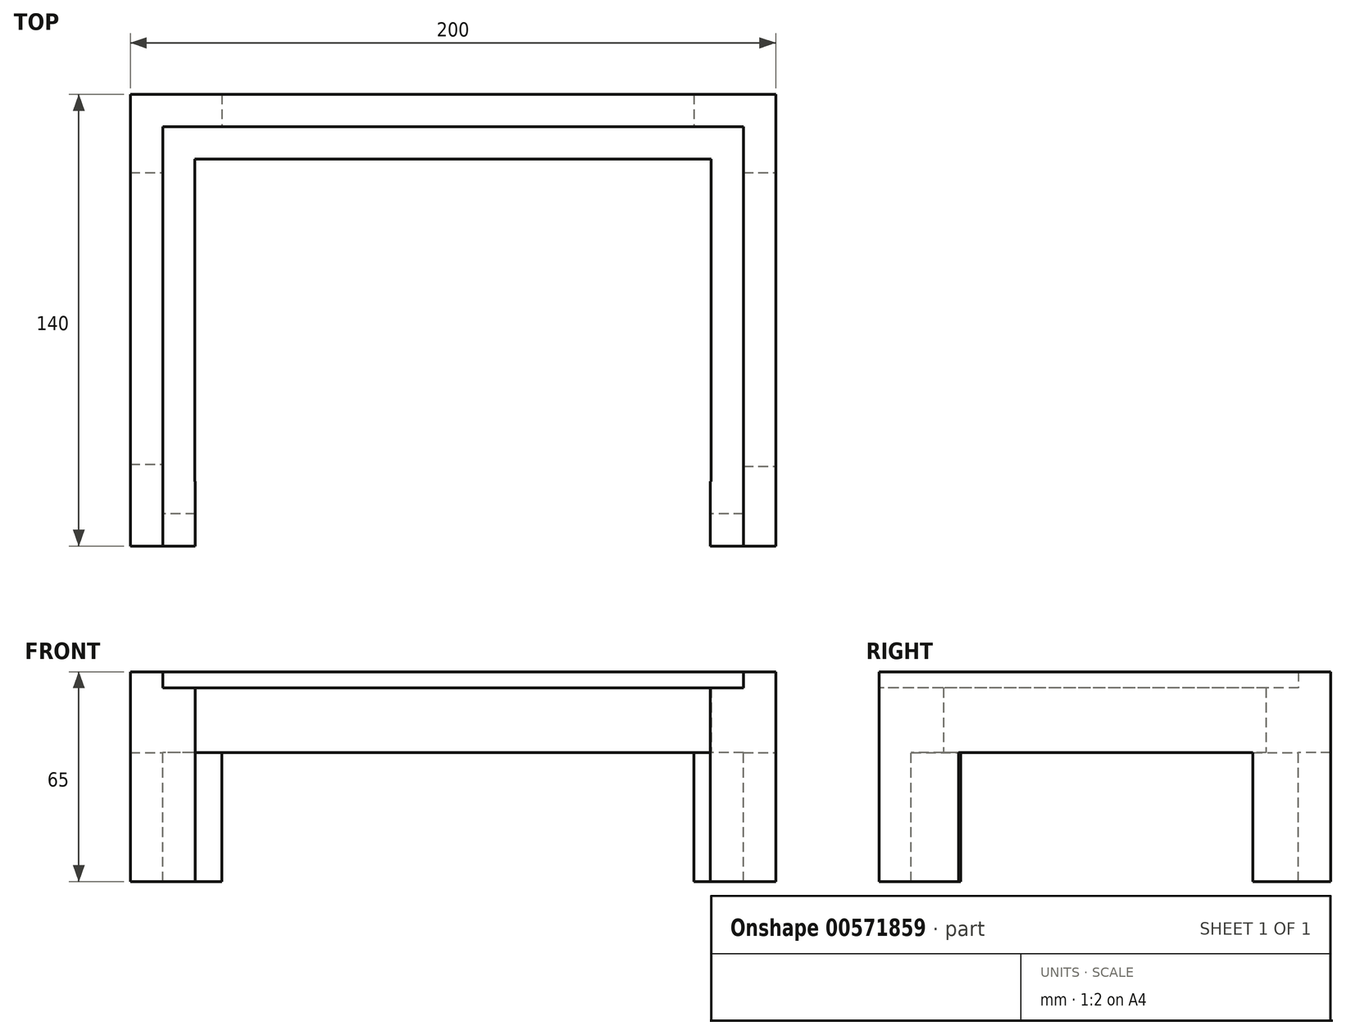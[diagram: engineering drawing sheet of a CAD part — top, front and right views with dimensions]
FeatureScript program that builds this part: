
annotation { "Feature Type Name" : "Feature", "Feature Type Description" : "" }
export const myFeature = defineFeature(function(context is Context, id is Id, definition is map)
    precondition{}
    {
        {
            var Q0;
            Q0=qCreatedBy(makeId("Top.planeOp"),FACE);
            var sketch = newSketch(context, id + "F0", { "sketchPlane" : qUnion([Q0])});
            skLineSegment(sketch, "E0.left", {"start": v(90, 0) * mm, "end": v(90, 0) * mm});
            skLineSegment(sketch, "E0.right", {"start": v(-90, 0) * mm, "end": v(-90, 0) * mm});
            skPoint(sketch, "E0.middle", {"position": v(0, 0) * mm});
            skLineSegment(sketch, "E1.bottom", {"start": v(100, -70) * mm, "end": v(-100, -70) * mm});
            skLineSegment(sketch, "E1.top", {"start": v(100, 70) * mm, "end": v(-100, 70) * mm});
            skLineSegment(sketch, "E1.left", {"start": v(100, -70) * mm, "end": v(100, 70) * mm});
            skLineSegment(sketch, "E1.right", {"start": v(-100, -70) * mm, "end": v(-100, 70) * mm});
            skLineSegment(sketch, "E2.bottom", {"start": v(90, -60) * mm, "end": v(-90, -60) * mm});
            skLineSegment(sketch, "E2.top", {"start": v(90, 60) * mm, "end": v(-90, 60) * mm});
            skLineSegment(sketch, "E2.left", {"start": v(90, -60) * mm, "end": v(90, 60) * mm});
            skLineSegment(sketch, "E2.right", {"start": v(-90, -60) * mm, "end": v(-90, 60) * mm});
            skLineSegment(sketch, "E3", {"start": v(-100, 45.82) * mm, "end": v(-90, 45.82) * mm});
            skLineSegment(sketch, "E4", {"start": v(-71.68, 70) * mm, "end": v(-71.68, 60) * mm});
            skLineSegment(sketch, "E5", {"start": v(-100, -44.62) * mm, "end": v(-90, -44.62) * mm});
            skLineSegment(sketch, "E6", {"start": v(90, -45.29) * mm, "end": v(100, -45.29) * mm});
            skLineSegment(sketch, "E7", {"start": v(74.62, 70) * mm, "end": v(74.62, 60) * mm});
            skLineSegment(sketch, "E8", {"start": v(90, 45.82) * mm, "end": v(100, 45.82) * mm});
            skLineSegment(sketch, "E9.bottom", {"start": v(80, 50) * mm, "end": v(-80, 50) * mm});
            skLineSegment(sketch, "E9.top", {"start": v(80, -50) * mm, "end": v(-80, -50) * mm});
            skLineSegment(sketch, "E9.left", {"start": v(80, 50) * mm, "end": v(80, -50) * mm});
            skLineSegment(sketch, "E9.right", {"start": v(-80, 50) * mm, "end": v(-80, -50) * mm});
            skLineSegment(sketch, "E10.bottom", {"start": v(79.75, -50) * mm, "end": v(-79.88, -50) * mm});
            skLineSegment(sketch, "E10.top", {"start": v(79.75, -70) * mm, "end": v(-79.88, -70) * mm});
            skLineSegment(sketch, "E10.left", {"start": v(79.75, -50) * mm, "end": v(79.75, -70) * mm});
            skLineSegment(sketch, "E10.right", {"start": v(-79.88, -50) * mm, "end": v(-79.88, -70) * mm});
            skLineSegment(sketch, "E11", {"start": v(-90, -60) * mm, "end": v(-90, -70) * mm});
            skLineSegment(sketch, "E12", {"start": v(90, -60) * mm, "end": v(90, -70) * mm});
            skSolve(sketch);
        }
        {
            var Q0;
            {var subQ4=sQuery(id+"F0.wireOp",EDGE,"E7");Q0=makeQuery(id+"F0.imprint","IMPRINT",FACE,{"disambiguationData":[TD([[makeQuery(id+"F0.imprint","IMPRINT",EDGE,{"derivedFrom":subQ4}),1.0]])]});}
            var Q1;
            {var subQ0=sQuery(id+"F0.wireOp",EDGE,"E6");Q1=makeQuery(id+"F0.imprint","IMPRINT",FACE,{"disambiguationData":[TD([[makeQuery(id+"F0.imprint","IMPRINT",EDGE,{"derivedFrom":subQ0}),1.0]])]});}
            var Q2;
            Q2=makeQuery(id+"F0.imprint","IMPRINT",FACE,{"disambiguationData":[TD([[makeQuery(id+"F0.imprint","IMPRINT",EDGE,{"derivedFrom":sQuery(id+"F0.wireOp",EDGE,"E9.bottom")}),-1.0]])]});
            var Q3;
            {var subQ0=sQuery(id+"F0.wireOp",EDGE,"E6");Q3=makeQuery(id+"F0.imprint","IMPRINT",FACE,{"disambiguationData":[TD([[makeQuery(id+"F0.imprint","IMPRINT",EDGE,{"derivedFrom":subQ0}),-1.0]])]});}
            var Q4;
            {var subQ3=sQuery(id+"F0.wireOp",EDGE,"E12");Q4=makeQuery(id+"F0.imprint","IMPRINT",FACE,{"disambiguationData":[TD([[makeQuery(id+"F0.imprint","IMPRINT",EDGE,{"derivedFrom":subQ3}),-1.0]])]});}
            var Q5;
            {var subQ0=sQuery(id+"F0.wireOp",EDGE,"E5");Q5=makeQuery(id+"F0.imprint","IMPRINT",FACE,{"disambiguationData":[TD([[makeQuery(id+"F0.imprint","IMPRINT",EDGE,{"derivedFrom":subQ0}),-1.0]])]});}
            var Q6;
            {var subQ3=sQuery(id+"F0.wireOp",EDGE,"E11");Q6=makeQuery(id+"F0.imprint","IMPRINT",FACE,{"disambiguationData":[TD([[makeQuery(id+"F0.imprint","IMPRINT",EDGE,{"derivedFrom":subQ3}),1.0]])]});}
            var Q7;
            {var subQ0=sQuery(id+"F0.wireOp",EDGE,"E3");Q7=makeQuery(id+"F0.imprint","IMPRINT",FACE,{"disambiguationData":[TD([[makeQuery(id+"F0.imprint","IMPRINT",EDGE,{"derivedFrom":subQ0}),-1.0]])]});}
            var Q8;
            {var subQ3=sQuery(id+"F0.wireOp",EDGE,"E3");Q8=makeQuery(id+"F0.imprint","IMPRINT",FACE,{"disambiguationData":[TD([[makeQuery(id+"F0.imprint","IMPRINT",EDGE,{"derivedFrom":subQ3}),1.0]])]});}
            var Q9;
            {var subQ0=sQuery(id+"F0.wireOp",EDGE,"E4");Q9=makeQuery(id+"F0.imprint","IMPRINT",FACE,{"disambiguationData":[TD([[makeQuery(id+"F0.imprint","IMPRINT",EDGE,{"derivedFrom":subQ0}),1.0]])]});}
            extrude(context, id + "F1", {"entities" : qUnion([Q0, Q1, Q2, Q3, Q4, Q5, Q6, Q7, Q8, Q9]), "depth" : 20 * mm, "offsetDistance" : 25 * mm});
        }
        {
            var Q0;
            {var subQ3=sQuery(id+"F0.wireOp",EDGE,"E3");Q0=makeQuery(id+"F0.imprint","IMPRINT",FACE,{"disambiguationData":[TD([[makeQuery(id+"F0.imprint","IMPRINT",EDGE,{"derivedFrom":subQ3}),1.0]])]});}
            var Q1;
            {var subQ0=sQuery(id+"F0.wireOp",EDGE,"E3");Q1=makeQuery(id+"F0.imprint","IMPRINT",FACE,{"disambiguationData":[TD([[makeQuery(id+"F0.imprint","IMPRINT",EDGE,{"derivedFrom":subQ0}),-1.0]])]});}
            var Q2;
            {var subQ0=sQuery(id+"F0.wireOp",EDGE,"E5");Q2=makeQuery(id+"F0.imprint","IMPRINT",FACE,{"disambiguationData":[TD([[makeQuery(id+"F0.imprint","IMPRINT",EDGE,{"derivedFrom":subQ0}),-1.0]])]});}
            var Q3;
            {var subQ0=sQuery(id+"F0.wireOp",EDGE,"E4");Q3=makeQuery(id+"F0.imprint","IMPRINT",FACE,{"disambiguationData":[TD([[makeQuery(id+"F0.imprint","IMPRINT",EDGE,{"derivedFrom":subQ0}),1.0]])]});}
            var Q4;
            {var subQ4=sQuery(id+"F0.wireOp",EDGE,"E7");Q4=makeQuery(id+"F0.imprint","IMPRINT",FACE,{"disambiguationData":[TD([[makeQuery(id+"F0.imprint","IMPRINT",EDGE,{"derivedFrom":subQ4}),1.0]])]});}
            var Q5;
            {var subQ0=sQuery(id+"F0.wireOp",EDGE,"E6");Q5=makeQuery(id+"F0.imprint","IMPRINT",FACE,{"disambiguationData":[TD([[makeQuery(id+"F0.imprint","IMPRINT",EDGE,{"derivedFrom":subQ0}),1.0]])]});}
            var Q6;
            {var subQ0=sQuery(id+"F0.wireOp",EDGE,"E6");Q6=makeQuery(id+"F0.imprint","IMPRINT",FACE,{"disambiguationData":[TD([[makeQuery(id+"F0.imprint","IMPRINT",EDGE,{"derivedFrom":subQ0}),-1.0]])]});}
            extrude(context, id + "F2", {"entities" : qUnion([Q0, Q1, Q2, Q3, Q4, Q5, Q6]), "operationType" : NewBodyOperationType.ADD, "depth" : 25 * mm, "offsetDistance" : 25 * mm});
        }
        {
            var Q0;
            {var subQ3=sQuery(id+"F0.wireOp",EDGE,"E3");Q0=makeQuery(id+"F0.imprint","IMPRINT",FACE,{"disambiguationData":[TD([[makeQuery(id+"F0.imprint","IMPRINT",EDGE,{"derivedFrom":subQ3}),1.0]])]});}
            var Q1;
            {var subQ0=sQuery(id+"F0.wireOp",EDGE,"E5");Q1=makeQuery(id+"F0.imprint","IMPRINT",FACE,{"disambiguationData":[TD([[makeQuery(id+"F0.imprint","IMPRINT",EDGE,{"derivedFrom":subQ0}),-1.0]])]});}
            var Q2;
            {var subQ3=sQuery(id+"F0.wireOp",EDGE,"E11");Q2=makeQuery(id+"F0.imprint","IMPRINT",FACE,{"disambiguationData":[TD([[makeQuery(id+"F0.imprint","IMPRINT",EDGE,{"derivedFrom":subQ3}),1.0]])]});}
            var Q3;
            {var subQ3=sQuery(id+"F0.wireOp",EDGE,"E12");Q3=makeQuery(id+"F0.imprint","IMPRINT",FACE,{"disambiguationData":[TD([[makeQuery(id+"F0.imprint","IMPRINT",EDGE,{"derivedFrom":subQ3}),-1.0]])]});}
            var Q4;
            {var subQ0=sQuery(id+"F0.wireOp",EDGE,"E6");Q4=makeQuery(id+"F0.imprint","IMPRINT",FACE,{"disambiguationData":[TD([[makeQuery(id+"F0.imprint","IMPRINT",EDGE,{"derivedFrom":subQ0}),-1.0]])]});}
            var Q5;
            {var subQ4=sQuery(id+"F0.wireOp",EDGE,"E7");Q5=makeQuery(id+"F0.imprint","IMPRINT",FACE,{"disambiguationData":[TD([[makeQuery(id+"F0.imprint","IMPRINT",EDGE,{"derivedFrom":subQ4}),1.0]])]});}
            extrude(context, id + "F3", {"entities" : qUnion([Q0, Q1, Q2, Q3, Q4, Q5]), "operationType" : NewBodyOperationType.ADD, "oppositeDirection" : true, "depth" : 40 * mm, "offsetDistance" : 25 * mm});
        }
    });
